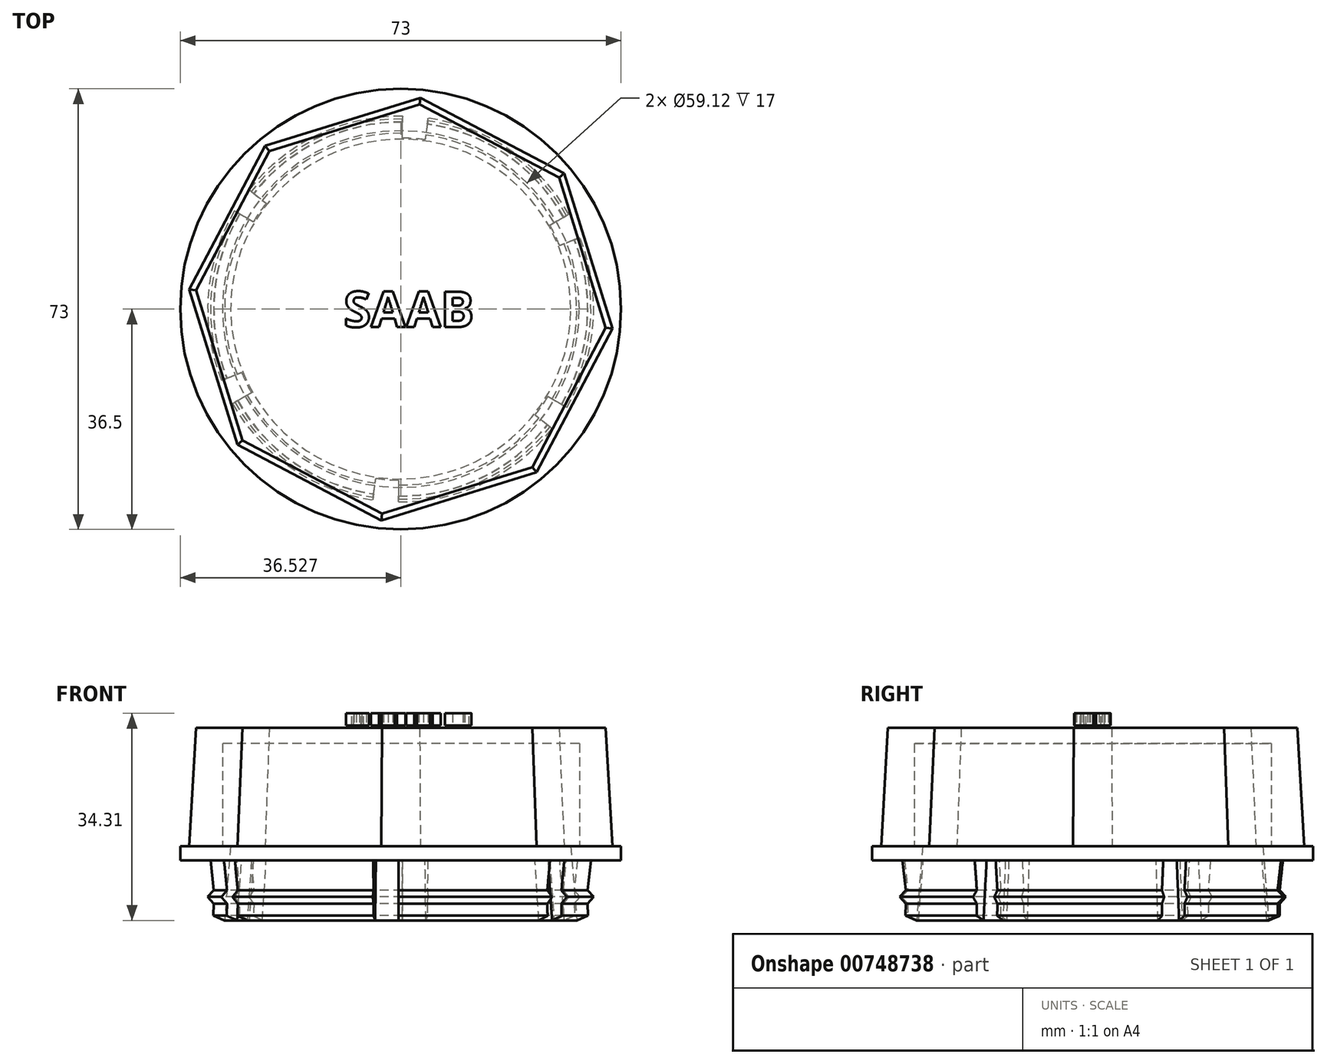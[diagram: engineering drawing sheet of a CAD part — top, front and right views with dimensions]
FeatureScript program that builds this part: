
annotation { "Feature Type Name" : "Feature", "Feature Type Description" : "" }
export const myFeature = defineFeature(function(context is Context, id is Id, definition is map)
    precondition{}
    {
        {
            var Q0;
            Q0=qCreatedBy(makeId("Top.planeOp"),FACE);
            var sketch = newSketch(context, id + "F0", { "sketchPlane" : qUnion([Q0])});
            skCircle(sketch, "E0.cCircle", {"center": v(41.88, 0) * mm, "radius": 35.18 * mm, "construction": true});
            skLineSegment(sketch, "E0.0", {"start": v(14.82, -22.49) * mm, "end": v(6.85, 3.23) * mm});
            skLineSegment(sketch, "E0.1", {"start": v(6.85, 3.23) * mm, "end": v(19.39, 27.05) * mm});
            skLineSegment(sketch, "E0.2", {"start": v(19.39, 27.05) * mm, "end": v(45.1, 35.03) * mm});
            skLineSegment(sketch, "E0.3", {"start": v(45.1, 35.03) * mm, "end": v(68.93, 22.49) * mm});
            skLineSegment(sketch, "E0.4", {"start": v(68.93, 22.49) * mm, "end": v(76.9, -3.23) * mm});
            skLineSegment(sketch, "E0.5", {"start": v(76.9, -3.23) * mm, "end": v(64.36, -27.05) * mm});
            skLineSegment(sketch, "E0.6", {"start": v(64.36, -27.05) * mm, "end": v(38.65, -35.03) * mm});
            skLineSegment(sketch, "E0.7", {"start": v(38.65, -35.03) * mm, "end": v(14.82, -22.49) * mm});
            skSolve(sketch);
        }
        {
            var Q0;
            Q0=qSketchRegion(id+"F0",true);
            extrude(context, id + "F1", {"entities" : qUnion([Q0]), "depth" : 19.6 * mm, "offsetDistance" : 25 * mm, "hasDraft" : true, "draftAngle" : 3 * degree, "draftPullDirection" : true});
        }
        {
            var Q0;
            Q0=qCreatedBy(makeId("Front.planeOp"),FACE);
            var sketch = newSketch(context, id + "F2", { "sketchPlane" : qUnion([Q0])});
            skLineSegment(sketch, "E1", {"start": v(71.3, 19.61) * mm, "end": v(71.3, 20.31) * mm});
            skLineSegment(sketch, "E2", {"start": v(71.3, 20.31) * mm, "end": v(70.7, 20.31) * mm});
            skLineSegment(sketch, "E3", {"start": v(70.7, 20.31) * mm, "end": v(70.7, 19.61) * mm});
            skLineSegment(sketch, "E4", {"start": v(61.4, 22) * mm, "end": v(61.4, 21.36) * mm});
            skLineSegment(sketch, "E5", {"start": v(61.4, 21.36) * mm, "end": v(41.94, 21.36) * mm});
            skArc(sketch, "E6", {"start": v(70.7, 19.61) * mm, "mid": v(66.19, 21.38) * mm, "end": v(61.4, 22) * mm});
            skLineSegment(sketch, "E7", {"start": v(41.94, 21.36) * mm, "end": v(41.94, 19.6) * mm});
            skSolve(sketch);
        }
        {
            var Q0;
            Q0=qSketchRegion(id+"F2",true);
            var Q1;
            Q1=sQuery(id+"F2.wireOp",EDGE,"E5");
            var Q2;
            Q2=sQuery(id+"F2.wireOp",EDGE,"E4");
            var Q3;
            Q3=sQuery(id+"F2.wireOp",EDGE,"E6");
            var Q4;
            Q4=sQuery(id+"F2.wireOp",EDGE,"E1");
            var Q5;
            Q5=sQuery(id+"F2.wireOp",EDGE,"E3");
            var Q6;
            Q6=sQuery(id+"F2.wireOp",EDGE,"E2");
            var Q7;
            Q7=sQuery(id+"F2.wireOp",EDGE,"E7");
            revolve(context, id + "F3", {"bodyType" : ToolBodyType.SURFACE, "surfaceOperationType" : NewSurfaceOperationType.NEW, "entities" : qUnion([Q0]), "surfaceEntities" : qUnion([Q1, Q2, Q3, Q4, Q5, Q6]), "axis" : qUnion([Q7]), "revolveType" : RevolveType.FULL});
        }
        {
            var Q0;
            Q0=qCreatedBy(makeId("Front.planeOp"),FACE);
            var sketch = newSketch(context, id + "F4", { "sketchPlane" : qUnion([Q0])});
            skLineSegment(sketch, "E8", {"start": v(41.85, 2.47) * mm, "end": v(41.85, -0.28) * mm});
            skLineSegment(sketch, "E9", {"start": v(13.92, 0) * mm, "end": v(10.66, 0) * mm});
            skLineSegment(sketch, "E10", {"start": v(13.7, 0) * mm, "end": v(12.7, -12.3) * mm});
            skLineSegment(sketch, "E11", {"start": v(12.7, -12.3) * mm, "end": v(10.85, -11.54) * mm});
            skLineSegment(sketch, "E12", {"start": v(10.85, -11.54) * mm, "end": v(10.9, -9.54) * mm});
            skLineSegment(sketch, "E13", {"start": v(9.9, -8.43) * mm, "end": v(10.9, -9.54) * mm});
            skLineSegment(sketch, "E14", {"start": v(9.9, -8.43) * mm, "end": v(10.9, -7.32) * mm});
            skLineSegment(sketch, "E15", {"start": v(10.9, -7.32) * mm, "end": v(10.35, -2.35) * mm});
            skLineSegment(sketch, "E16", {"start": v(41.85, 0) * mm, "end": v(5.35, 0) * mm});
            skLineSegment(sketch, "E17", {"start": v(41.85, 2.47) * mm, "end": v(41.85, -22.81) * mm});
            skPoint(sketch, "E18", {"position": v(5.35, -2.35) * mm});
            skLineSegment(sketch, "E19", {"start": v(5.35, -2.35) * mm, "end": v(10.35, -2.35) * mm});
            skLineSegment(sketch, "E20", {"start": v(5.35, 0) * mm, "end": v(5.35, -2.35) * mm});
            skPoint(sketch, "E21", {"position": v(10.85, 0) * mm});
            skSolve(sketch);
        }
        {
            var Q0;
            Q0=qSketchRegion(id+"F4",true);
            var Q1;
            Q1=sQuery(id+"F4.wireOp",EDGE,"E16");
            var Q2;
            Q2=sQuery(id+"F4.wireOp",EDGE,"4cd7ZZWE-5ar5-vtm7-FDXw-HXyrbe5Stu3w");
            var Q3;
            Q3=sQuery(id+"F4.wireOp",EDGE,"E15");
            var Q4;
            Q4=sQuery(id+"F4.wireOp",EDGE,"E14");
            var Q5;
            Q5=sQuery(id+"F4.wireOp",EDGE,"E13");
            var Q6;
            Q6=sQuery(id+"F4.wireOp",EDGE,"E11");
            var Q7;
            Q7=sQuery(id+"F4.wireOp",EDGE,"E12");
            var Q8;
            Q8=sQuery(id+"F4.wireOp",EDGE,"E10");
            var Q9;
            Q9=sQuery(id+"F4.wireOp",EDGE,"E17");
            revolve(context, id + "F5", {"surfaceOperationType" : NewSurfaceOperationType.NEW, "entities" : qUnion([Q0]), "surfaceEntities" : qUnion([Q1, Q2, Q3, Q4, Q5, Q6, Q7, Q8]), "axis" : qUnion([Q9]), "revolveType" : RevolveType.FULL});
        }
        {
            var Q0;
            Q0=qCreatedBy(makeId("Top.planeOp"),FACE);
            var sketch = newSketch(context, id + "F6", { "sketchPlane" : qUnion([Q0])});
            skLineSegment(sketch, "E22", {"start": v(41.81, 0) * mm, "end": v(7.56, 20.28) * mm});
            skLineSegment(sketch, "E23", {"start": v(7.56, 20.28) * mm, "end": v(10.73, 24.52) * mm});
            skLineSegment(sketch, "E24", {"start": v(10.73, 24.52) * mm, "end": v(41.81, 0) * mm});
            skLineSegment(sketch, "E25.1.0", {"start": v(41.81, 0) * mm, "end": v(7.13, -19.52) * mm});
            skLineSegment(sketch, "E25.1.1", {"start": v(7.13, -19.52) * mm, "end": v(5.04, -14.66) * mm});
            skLineSegment(sketch, "E25.1.2", {"start": v(5.04, -14.66) * mm, "end": v(41.81, 0) * mm});
            skLineSegment(sketch, "E25.2.0", {"start": v(41.81, 0) * mm, "end": v(41.38, -39.8) * mm});
            skLineSegment(sketch, "E25.2.1", {"start": v(41.38, -39.8) * mm, "end": v(36.12, -39.18) * mm});
            skLineSegment(sketch, "E25.2.2", {"start": v(36.12, -39.18) * mm, "end": v(41.81, 0) * mm});
            skLineSegment(sketch, "E25.3.0", {"start": v(41.81, 0) * mm, "end": v(76.07, -20.28) * mm});
            skLineSegment(sketch, "E25.3.1", {"start": v(76.07, -20.28) * mm, "end": v(72.9, -24.52) * mm});
            skLineSegment(sketch, "E25.3.2", {"start": v(72.9, -24.52) * mm, "end": v(41.81, 0) * mm});
            skLineSegment(sketch, "E25.4.0", {"start": v(41.81, 0) * mm, "end": v(76.5, 19.52) * mm});
            skLineSegment(sketch, "E25.4.1", {"start": v(76.5, 19.52) * mm, "end": v(78.6, 14.66) * mm});
            skLineSegment(sketch, "E25.4.2", {"start": v(78.6, 14.66) * mm, "end": v(41.81, 0) * mm});
            skLineSegment(sketch, "E25.5.0", {"start": v(41.81, 0) * mm, "end": v(42.25, 39.8) * mm});
            skLineSegment(sketch, "E25.5.1", {"start": v(42.25, 39.8) * mm, "end": v(47.5, 39.18) * mm});
            skLineSegment(sketch, "E25.5.2", {"start": v(47.5, 39.18) * mm, "end": v(41.81, 0) * mm});
            skPoint(sketch, "E25.center", {"position": v(41.81, 0) * mm});
            skSolve(sketch);
        }
        {
            var Q0;
            Q0=qSketchRegion(id+"F6",true);
            extrude(context, id + "F7", {"entities" : qUnion([Q0]), "oppositeDirection" : true, "depth" : 35 * mm, "offsetDistance" : 25 * mm});
        }
        {
            var Q0;
            Q0=makeQuery(id+"F7.opExtrude","SWEPT_BODY",BODY,{"disambiguationData":[OSD([sQuery(id+"F6.wireOp",EDGE,"E25.5.0"),sQuery(id+"F6.wireOp",EDGE,"E25.5.1"),sQuery(id+"F6.wireOp",EDGE,"E25.5.2")])]});
            var Q1;
            Q1=makeQuery(id+"F7.opExtrude","SWEPT_BODY",BODY,{"disambiguationData":[OSD([sQuery(id+"F6.wireOp",EDGE,"E25.4.0"),sQuery(id+"F6.wireOp",EDGE,"E25.4.1"),sQuery(id+"F6.wireOp",EDGE,"E25.4.2")])]});
            var Q2;
            Q2=makeQuery(id+"F7.opExtrude","SWEPT_BODY",BODY,{"disambiguationData":[OSD([sQuery(id+"F6.wireOp",EDGE,"E25.3.0"),sQuery(id+"F6.wireOp",EDGE,"E25.3.1"),sQuery(id+"F6.wireOp",EDGE,"E25.3.2")])]});
            var Q3;
            Q3=makeQuery(id+"F7.opExtrude","SWEPT_BODY",BODY,{"disambiguationData":[OSD([sQuery(id+"F6.wireOp",EDGE,"E25.2.0"),sQuery(id+"F6.wireOp",EDGE,"E25.2.1"),sQuery(id+"F6.wireOp",EDGE,"E25.2.2")])]});
            var Q4;
            Q4=makeQuery(id+"F7.opExtrude","SWEPT_BODY",BODY,{"disambiguationData":[OSD([sQuery(id+"F6.wireOp",EDGE,"E25.1.0"),sQuery(id+"F6.wireOp",EDGE,"E25.1.1"),sQuery(id+"F6.wireOp",EDGE,"E25.1.2")])]});
            var Q5;
            Q5=makeQuery(id+"F7.opExtrude","SWEPT_BODY",BODY,{"disambiguationData":[OSD([sQuery(id+"F6.wireOp",EDGE,"E22"),sQuery(id+"F6.wireOp",EDGE,"E23"),sQuery(id+"F6.wireOp",EDGE,"E24")])]});
            var Q6;
            Q6=makeQuery(id+"F5.opRevolve","SWEPT_BODY",BODY,{"disambiguationData":[OSD([sQuery(id+"F4.wireOp",EDGE,"E10"),sQuery(id+"F4.wireOp",EDGE,"E11"),sQuery(id+"F4.wireOp",EDGE,"E12"),sQuery(id+"F4.wireOp",EDGE,"E13"),sQuery(id+"F4.wireOp",EDGE,"E14"),sQuery(id+"F4.wireOp",EDGE,"E15"),sQuery(id+"F4.wireOp",EDGE,"4cd7ZZWE-5ar5-vtm7-FDXw-HXyrbe5Stu3w"),sQuery(id+"F4.wireOp",EDGE,"E16")])]});
            var Q7;
            Q7=makeQuery(id+"F7.opExtrude","CAP_FACE",FACE,{"disambiguationData":[OSD([sQuery(id+"F6.wireOp",EDGE,"E25.5.0"),sQuery(id+"F6.wireOp",EDGE,"E25.5.1"),sQuery(id+"F6.wireOp",EDGE,"E25.5.2")])],"isStart":true});
            var Q8;
            Q8=makeQuery(id+"F7.opExtrude","CAP_FACE",FACE,{"disambiguationData":[OSD([sQuery(id+"F6.wireOp",EDGE,"E22"),sQuery(id+"F6.wireOp",EDGE,"E23"),sQuery(id+"F6.wireOp",EDGE,"E24")])],"isStart":true});
            var Q9;
            Q9=makeQuery(id+"F7.opExtrude","CAP_FACE",FACE,{"disambiguationData":[OSD([sQuery(id+"F6.wireOp",EDGE,"E25.1.0"),sQuery(id+"F6.wireOp",EDGE,"E25.1.1"),sQuery(id+"F6.wireOp",EDGE,"E25.1.2")])],"isStart":true});
            var Q10;
            Q10=makeQuery(id+"F7.opExtrude","CAP_FACE",FACE,{"disambiguationData":[OSD([sQuery(id+"F6.wireOp",EDGE,"E25.2.0"),sQuery(id+"F6.wireOp",EDGE,"E25.2.1"),sQuery(id+"F6.wireOp",EDGE,"E25.2.2")])],"isStart":true});
            var Q11;
            Q11=makeQuery(id+"F7.opExtrude","CAP_FACE",FACE,{"disambiguationData":[OSD([sQuery(id+"F6.wireOp",EDGE,"E25.3.0"),sQuery(id+"F6.wireOp",EDGE,"E25.3.1"),sQuery(id+"F6.wireOp",EDGE,"E25.3.2")])],"isStart":true});
            var Q12;
            Q12=makeQuery(id+"F7.opExtrude","CAP_FACE",FACE,{"disambiguationData":[OSD([sQuery(id+"F6.wireOp",EDGE,"E25.4.0"),sQuery(id+"F6.wireOp",EDGE,"E25.4.1"),sQuery(id+"F6.wireOp",EDGE,"E25.4.2")])],"isStart":true});
            booleanBodies(context, id + "F8", {"operationType" : BooleanOperationType.SUBTRACTION, "tools" : qUnion([Q0, Q1, Q2, Q3, Q4, Q5]), "targets" : qUnion([Q6]), "offset" : true, "entitiesToOffset" : qUnion([Q7, Q8, Q9, Q10, Q11, Q12]), "offsetDistance" : 2.35 * mm, "oppositeDirection" : true});
        }
        {
            var Q0;
            Q0=qCreatedBy(makeId("Top.planeOp"),FACE);
            var sketch = newSketch(context, id + "F9", { "sketchPlane" : qUnion([Q0])});
            skCircle(sketch, "E26", {"center": v(41.88, 0) * mm, "radius": 29.56 * mm});
            skSolve(sketch);
        }
        {
            var Q0;
            Q0=qSketchRegion(id+"F9",true);
            extrude(context, id + "F10", {"entities" : qUnion([Q0]), "operationType" : NewBodyOperationType.REMOVE, "depth" : 17 * mm, "offsetDistance" : 25 * mm});
        }
        {
            var Q0;
            Q0=qCreatedBy(makeId("Top.planeOp"),FACE);
            var sketch = newSketch(context, id + "F11", { "sketchPlane" : qUnion([Q0])});
            skText(sketch, "E27", { "text": "SAAB", "fontName": "OpenSans-Bold.ttf"});
            const initialGuessF11  = {"E27": [0.03239, -0.00298, 1, 0, 0.00593]};
            skSetInitialGuess(sketch, initialGuessF11);
            skSolve(sketch);
        }
        {
            var Q0;
            Q0=qSketchRegion(id+"F11",true);
            extrude(context, id + "F12", {"entities" : qUnion([Q0]), "depth" : 2 * mm, "offsetDistance" : 25 * mm});
        }
        {
            var Q0;
            Q0=makeQuery(id+"F12.opExtrude","SWEPT_BODY",BODY,{"disambiguationData":[OSD([sQuery(id+"F11.wireOp",EDGE,"E27.sketch_text.stroke-0"),sQuery(id+"F11.wireOp",EDGE,"E27.sketch_text.stroke-1"),sQuery(id+"F11.wireOp",EDGE,"E27.sketch_text.stroke-2"),sQuery(id+"F11.wireOp",EDGE,"E27.sketch_text.stroke-3"),sQuery(id+"F11.wireOp",EDGE,"E27.sketch_text.stroke-4"),sQuery(id+"F11.wireOp",EDGE,"E27.sketch_text.stroke-5"),sQuery(id+"F11.wireOp",EDGE,"E27.sketch_text.stroke-6"),sQuery(id+"F11.wireOp",EDGE,"E27.sketch_text.stroke-7"),sQuery(id+"F11.wireOp",EDGE,"E27.sketch_text.stroke-8"),sQuery(id+"F11.wireOp",EDGE,"E27.sketch_text.stroke-9"),sQuery(id+"F11.wireOp",EDGE,"E27.sketch_text.stroke-10"),sQuery(id+"F11.wireOp",EDGE,"E27.sketch_text.stroke-11"),sQuery(id+"F11.wireOp",EDGE,"E27.sketch_text.stroke-12"),sQuery(id+"F11.wireOp",EDGE,"E27.sketch_text.stroke-13"),sQuery(id+"F11.wireOp",EDGE,"E27.sketch_text.stroke-14"),sQuery(id+"F11.wireOp",EDGE,"E27.sketch_text.stroke-15"),sQuery(id+"F11.wireOp",EDGE,"E27.sketch_text.stroke-16"),sQuery(id+"F11.wireOp",EDGE,"E27.sketch_text.stroke-17"),sQuery(id+"F11.wireOp",EDGE,"E27.sketch_text.stroke-18"),sQuery(id+"F11.wireOp",EDGE,"E27.sketch_text.stroke-19"),sQuery(id+"F11.wireOp",EDGE,"E27.sketch_text.stroke-20"),sQuery(id+"F11.wireOp",EDGE,"E27.sketch_text.stroke-21"),sQuery(id+"F11.wireOp",EDGE,"E27.sketch_text.stroke-22"),sQuery(id+"F11.wireOp",EDGE,"E27.sketch_text.stroke-23"),sQuery(id+"F11.wireOp",EDGE,"E27.sketch_text.stroke-24"),sQuery(id+"F11.wireOp",EDGE,"E27.sketch_text.stroke-25"),sQuery(id+"F11.wireOp",EDGE,"E27.sketch_text.stroke-26"),sQuery(id+"F11.wireOp",EDGE,"E27.sketch_text.stroke-27")])]});
            var Q1;
            Q1=makeQuery(id+"F12.opExtrude","SWEPT_BODY",BODY,{"disambiguationData":[OSD([sQuery(id+"F11.wireOp",EDGE,"E27.sketch_text.stroke-28"),sQuery(id+"F11.wireOp",EDGE,"E27.sketch_text.stroke-29"),sQuery(id+"F11.wireOp",EDGE,"E27.sketch_text.stroke-30"),sQuery(id+"F11.wireOp",EDGE,"E27.sketch_text.stroke-31"),sQuery(id+"F11.wireOp",EDGE,"E27.sketch_text.stroke-32"),sQuery(id+"F11.wireOp",EDGE,"E27.sketch_text.stroke-33"),sQuery(id+"F11.wireOp",EDGE,"E27.sketch_text.stroke-34"),sQuery(id+"F11.wireOp",EDGE,"E27.sketch_text.stroke-35"),sQuery(id+"F11.wireOp",EDGE,"E27.sketch_text.stroke-36"),sQuery(id+"F11.wireOp",EDGE,"E27.sketch_text.stroke-37"),sQuery(id+"F11.wireOp",EDGE,"E27.sketch_text.stroke-38"),sQuery(id+"F11.wireOp",EDGE,"E27.sketch_text.stroke-39")])]});
            var Q2;
            Q2=makeQuery(id+"F12.opExtrude","SWEPT_BODY",BODY,{"disambiguationData":[OSD([sQuery(id+"F11.wireOp",EDGE,"E27.sketch_text.stroke-40"),sQuery(id+"F11.wireOp",EDGE,"E27.sketch_text.stroke-41"),sQuery(id+"F11.wireOp",EDGE,"E27.sketch_text.stroke-42"),sQuery(id+"F11.wireOp",EDGE,"E27.sketch_text.stroke-43"),sQuery(id+"F11.wireOp",EDGE,"E27.sketch_text.stroke-44"),sQuery(id+"F11.wireOp",EDGE,"E27.sketch_text.stroke-45"),sQuery(id+"F11.wireOp",EDGE,"E27.sketch_text.stroke-46"),sQuery(id+"F11.wireOp",EDGE,"E27.sketch_text.stroke-47"),sQuery(id+"F11.wireOp",EDGE,"E27.sketch_text.stroke-48"),sQuery(id+"F11.wireOp",EDGE,"E27.sketch_text.stroke-49"),sQuery(id+"F11.wireOp",EDGE,"E27.sketch_text.stroke-50"),sQuery(id+"F11.wireOp",EDGE,"E27.sketch_text.stroke-51")])]});
            var Q3;
            Q3=makeQuery(id+"F12.opExtrude","SWEPT_BODY",BODY,{"disambiguationData":[OSD([sQuery(id+"F11.wireOp",EDGE,"E27.sketch_text.stroke-52"),sQuery(id+"F11.wireOp",EDGE,"E27.sketch_text.stroke-53"),sQuery(id+"F11.wireOp",EDGE,"E27.sketch_text.stroke-54"),sQuery(id+"F11.wireOp",EDGE,"E27.sketch_text.stroke-55"),sQuery(id+"F11.wireOp",EDGE,"E27.sketch_text.stroke-56"),sQuery(id+"F11.wireOp",EDGE,"E27.sketch_text.stroke-57"),sQuery(id+"F11.wireOp",EDGE,"E27.sketch_text.stroke-58"),sQuery(id+"F11.wireOp",EDGE,"E27.sketch_text.stroke-59"),sQuery(id+"F11.wireOp",EDGE,"E27.sketch_text.stroke-60"),sQuery(id+"F11.wireOp",EDGE,"E27.sketch_text.stroke-61"),sQuery(id+"F11.wireOp",EDGE,"E27.sketch_text.stroke-62"),sQuery(id+"F11.wireOp",EDGE,"E27.sketch_text.stroke-63"),sQuery(id+"F11.wireOp",EDGE,"E27.sketch_text.stroke-64"),sQuery(id+"F11.wireOp",EDGE,"E27.sketch_text.stroke-65"),sQuery(id+"F11.wireOp",EDGE,"E27.sketch_text.stroke-66"),sQuery(id+"F11.wireOp",EDGE,"E27.sketch_text.stroke-67"),sQuery(id+"F11.wireOp",EDGE,"E27.sketch_text.stroke-68"),sQuery(id+"F11.wireOp",EDGE,"E27.sketch_text.stroke-69"),sQuery(id+"F11.wireOp",EDGE,"E27.sketch_text.stroke-70"),sQuery(id+"F11.wireOp",EDGE,"E27.sketch_text.stroke-71"),sQuery(id+"F11.wireOp",EDGE,"E27.sketch_text.stroke-72"),sQuery(id+"F11.wireOp",EDGE,"E27.sketch_text.stroke-73"),sQuery(id+"F11.wireOp",EDGE,"E27.sketch_text.stroke-74"),sQuery(id+"F11.wireOp",EDGE,"E27.sketch_text.stroke-75"),sQuery(id+"F11.wireOp",EDGE,"E27.sketch_text.stroke-76")])]});
            transform(context, id + "F13", {"entities" : qUnion([Q0, Q1, Q2, Q3]), "transformType" : TransformType.TRANSLATION_3D, "dx" : 0 * mm, "dy" : 0 * mm, "dz" : 20 * mm, "makeCopy" : false});
        }
    });
